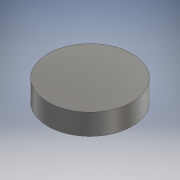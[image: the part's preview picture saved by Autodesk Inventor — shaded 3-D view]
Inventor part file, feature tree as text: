
AUTODESK INVENTOR PART (.ipt)
format: ipt  version: 2017.3 (Build 213256000, 256)  size: 95,744 bytes
history: native  units: mm
features: sheet_metal_op x1, sketch x1, other x1
ambient origin geometry x8: Origin, YZ Plane, XZ Plane, XY Plane, X Axis, Y Axis, Z Axis, Center Point
bodies: Solid1 (feature_tree)
feature tree (3):
  sheet_metal_op  "Face1"
  sketch  "Sketch1"  dims[d0=20.0mm d1=5.0mm]
  other  "Plate1"
